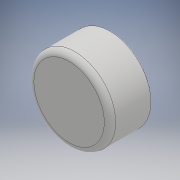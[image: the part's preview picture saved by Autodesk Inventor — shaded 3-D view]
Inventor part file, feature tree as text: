
AUTODESK INVENTOR PART (.ipt)
format: ipt  version: 2018 (Build 220112000, 112)  size: 138,240 bytes
history: native  units: mm
features: extrude x2, fillet x2, sketch x2, thread x1
ambient origin geometry x8: Origin, YZ Plane, XZ Plane, XY Plane, X Axis, Y Axis, Z Axis, Center Point
bodies: Solid1 (feature_tree)
feature tree (7):
  extrude  "Extrusion1"  Depth=11.0mm TaperAngle=0.0deg
  extrude  "Extrusion2"  Depth=10.0mm TaperAngle=0.0deg
  fillet  "Fillet1"  Radius=1.5mm
  fillet  "Fillet2"  Radius=0.25mm
  thread  "Thread1"  [1 undecoded]
  sketch  "Sketch1"  dims[d0=21.5mm d1=11.0mm d2=0.0mm]
  sketch  "Sketch2"  dims[d3=20.0mm d4=10.0mm d5=0.0mm d6=1.5mm d7=0.25mm d8=10.0mm d9=0.0mm]
note: 1 required parameter value undecoded (feature->parameter linkage not recoverable at this tier; creation-order binding heuristic only, values carry confidence <= 0.55)
